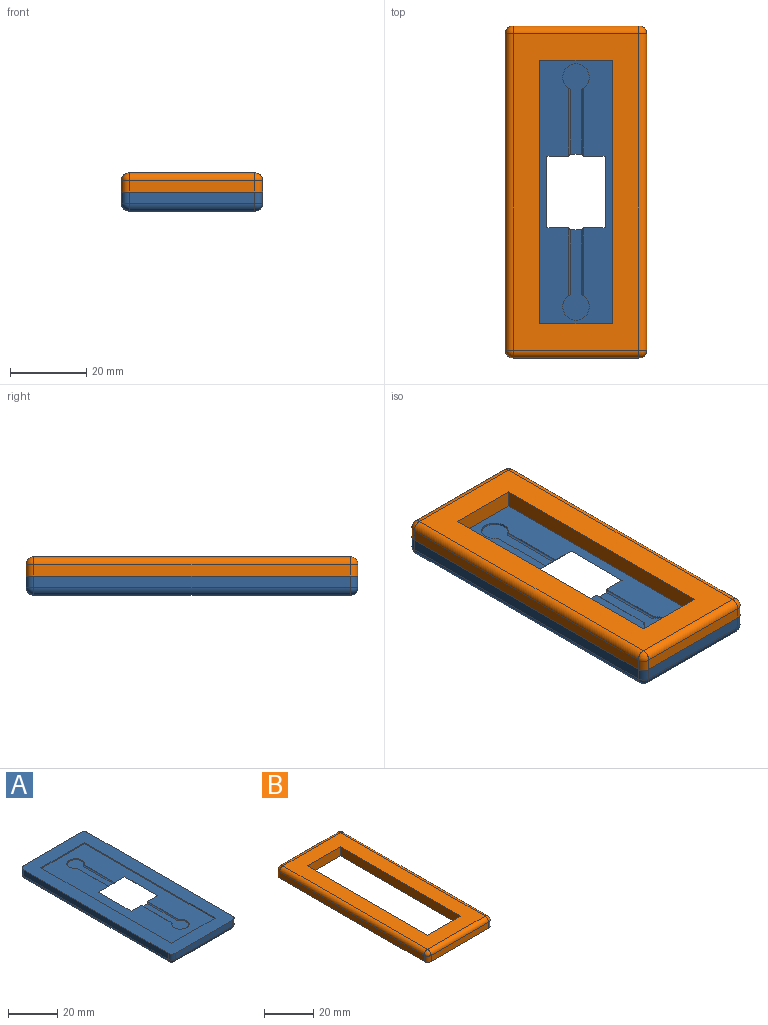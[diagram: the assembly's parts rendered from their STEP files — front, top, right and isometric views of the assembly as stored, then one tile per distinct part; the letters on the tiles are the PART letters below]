
ASSEMBLY  parts=2 mates=1
PART A: 35 faces, bbox 37x87x5 mm
  f0: plane 75x25mm, normal (0,0,1), area 1381.6mm2, adj f1,f2,f9,f10,f11,f12,f25,f26
  f1: plane 24.23x4.5mm, normal (0,0.71,-0.71), area 123.1mm2, adj f0,f3,f25,f26,f29,f31,f32
  f2: plane 24.23x4.5mm, normal (0,-0.71,-0.71), area 123.1mm2, adj f0,f3,f25,f26,f27,f33,f34
  f3: plane 83x33mm, normal (0,0,-1), area 2064.7mm2, adj f1,f2,f16,f17,f21,f22,f25,f26
  f4: plane 87x37mm, normal (0,0,1), area 1340.6mm2, adj f5,f6,f7,f8,f9,f10,f11,f12
  f5: plane 83x3mm, normal (1,0,0), area 249mm2, adj f4,f15,f21,f24
  f6: plane 33x3mm, normal (0,-1,0), area 99mm2, adj f4,f18,f22,f24
  f7: plane 83x3mm, normal (-1,0,0), area 249mm2, adj f4,f13,f17,f18
  f8: plane 33x3mm, normal (0,1,0), area 99mm2, adj f4,f13,f15,f16
  f9: plane 75x0.5mm, normal (-1,0,0), area 37.5mm2, adj f0,f4,f10,f12
  f10: plane 25x0.5mm, normal (0,-1,0), area 12.5mm2, adj f0,f4,f9,f11
  f11: plane 75x0.5mm, normal (1,0,0), area 37.5mm2, adj f0,f4,f10,f12
  f12: plane 25x0.5mm, normal (0,1,0), area 12.5mm2, adj f0,f4,f9,f11
  f13: cylinder r=2mm len=3mm, axis (0,0,-1), area 9.4mm2, adj f4,f7,f8,f14
  f14: sphere r=2mm, area 6.3mm2, adj f13,f16,f17
  f15: cylinder r=2mm len=3mm, axis (0,0,1), area 9.4mm2, adj f4,f5,f8,f19
  f16: cylinder r=2mm len=33mm, axis (-1,0,0), area 103.7mm2, adj f3,f8,f14,f19
  f17: cylinder r=2mm len=83mm, axis (0,-1,0), area 260.8mm2, adj f3,f7,f14,f20
  f18: cylinder r=2mm len=3mm, axis (0,0,1), area 9.4mm2, adj f4,f6,f7,f20
  f19: sphere r=2mm, area 6.3mm2, adj f15,f16,f21
  f20: sphere r=2mm, area 6.3mm2, adj f17,f18,f22
  f21: cylinder r=2mm len=83mm, axis (0,1,0), area 260.8mm2, adj f3,f5,f19,f23
  f22: cylinder r=2mm len=33mm, axis (1,0,0), area 103.7mm2, adj f3,f6,f20,f23
  f23: sphere r=2mm, area 6.3mm2, adj f21,f22,f24
  f24: cylinder r=2mm len=3mm, axis (0,0,-1), area 9.4mm2, adj f4,f5,f6,f23
  f25: plane 27.82x4.5mm, normal (-0.71,0,-0.71), area 148.4mm2, adj f0,f1,f2,f3
  f26: plane 27.82x4.5mm, normal (0.71,0,-0.71), area 148.4mm2, adj f0,f1,f2,f3
  f27: plane 23.67x6.97mm, normal (0,0,1), area 84.4mm2, adj f2,f28,f33,f34
  f28: cylinder r=3.48mm len=6.97mm, axis (0,0,1), area 9.1mm2, adj f0,f27,f33,f34
  f29: plane 23.67x6.97mm, normal (0,0,1), area 84.4mm2, adj f1,f30,f31,f32
  f30: cylinder r=3.48mm len=6.97mm, axis (0,0,1), area 9.1mm2, adj f0,f29,f31,f32
  f31: cylinder r=0.5mm len=17.75mm, axis (0,-1,0), area 13.6mm2, adj f0,f1,f29,f30
  f32: cylinder r=0.5mm len=17.75mm, axis (0,1,0), area 13.6mm2, adj f0,f1,f29,f30
  f33: cylinder r=0.5mm len=17.75mm, axis (0,-1,0), area 13.6mm2, adj f0,f2,f27,f28
  f34: cylinder r=0.5mm len=17.75mm, axis (0,1,0), area 13.6mm2, adj f0,f2,f27,f28
PART B: 37 faces, bbox 37x87x5 mm
  f0: plane 87x37mm, normal (0,0,-1), area 1212.6mm2, adj f1,f2,f3,f8,f10,f12,f15,f21
  f1: plane 33x3mm, normal (0,1,0), area 99mm2, adj f0,f12,f18,f21
  f2: plane 83x3mm, normal (-1,0,0), area 249mm2, adj f0,f15,f19,f21
  f3: plane 33x3mm, normal (0,-1,0), area 99mm2, adj f0,f10,f14,f15
  f4: plane 69x4.5mm, normal (1,0,0), area 310.5mm2, adj f5,f7,f9,f26
  f5: plane 19x4.5mm, normal (0,-1,0), area 85.5mm2, adj f4,f6,f9,f26
  f6: plane 69x4.5mm, normal (-1,0,0), area 310.5mm2, adj f5,f7,f9,f26
  f7: plane 19x4.5mm, normal (0,1,0), area 85.5mm2, adj f4,f6,f9,f26
  f8: plane 83x3mm, normal (1,0,0), area 249mm2, adj f0,f10,f12,f13
  f9: plane 83x33mm, normal (0,0,1), area 1428mm2, adj f4,f5,f6,f7,f13,f14,f18,f19
  f10: cylinder r=2mm len=3mm, axis (0,0,-1), area 9.4mm2, adj f0,f3,f8,f11
  f11: sphere r=2mm, area 6.3mm2, adj f10,f13,f14
  f12: cylinder r=2mm len=3mm, axis (0,0,-1), area 9.4mm2, adj f0,f1,f8,f16
  f13: cylinder r=2mm len=83mm, axis (0,-1,0), area 260.8mm2, adj f8,f9,f11,f16
  f14: cylinder r=2mm len=33mm, axis (-1,0,0), area 103.7mm2, adj f3,f9,f11,f17
  f15: cylinder r=2mm len=3mm, axis (0,0,-1), area 9.4mm2, adj f0,f2,f3,f17
  f16: sphere r=2mm, area 6.3mm2, adj f12,f13,f18
  f17: sphere r=2mm, area 6.3mm2, adj f14,f15,f19
  f18: cylinder r=2mm len=33mm, axis (1,0,0), area 103.7mm2, adj f1,f9,f16,f20
  f19: cylinder r=2mm len=83mm, axis (0,1,0), area 260.8mm2, adj f2,f9,f17,f20
  f20: sphere r=2mm, area 6.3mm2, adj f18,f19,f21
  f21: cylinder r=2mm len=3mm, axis (0,0,-1), area 9.4mm2, adj f0,f1,f2,f20
  f22: plane 25x0.5mm, normal (0,-1,0), area 12.5mm2, adj f0,f23,f25,f26
  f23: plane 75x0.5mm, normal (1,0,0), area 37.5mm2, adj f0,f22,f24,f26
  f24: plane 25x0.5mm, normal (0,1,0), area 12.5mm2, adj f0,f23,f25,f26
  f25: plane 75x0.5mm, normal (-1,0,0), area 37.5mm2, adj f0,f22,f24,f26
  f26: plane 75x25mm, normal (0,0,-1), area 564mm2, adj f4,f5,f6,f7,f22,f23,f24,f25
  f27: plane 3.35x3.35mm, normal (1,0,0), area 11.2mm2, adj f0,f28,f30,f31
  f28: plane 19.1x3.35mm, normal (0,-1,0), area 64mm2, adj f0,f27,f29,f31
  f29: plane 3.35x3.35mm, normal (-1,0,0), area 11.2mm2, adj f0,f28,f30,f31
  f30: plane 19.1x3.35mm, normal (0,1,0), area 64mm2, adj f0,f27,f29,f31
  f31: plane 19.1x3.35mm, normal (0,0,-1), area 64mm2, adj f27,f28,f29,f30
  f32: plane 3.35x3.35mm, normal (1,0,0), area 11.2mm2, adj f0,f33,f35,f36
  f33: plane 19.1x3.35mm, normal (0,-1,0), area 64mm2, adj f0,f32,f34,f36
  f34: plane 3.35x3.35mm, normal (-1,0,0), area 11.2mm2, adj f0,f33,f35,f36
  f35: plane 19.1x3.35mm, normal (0,1,0), area 64mm2, adj f0,f32,f34,f36
  f36: plane 19.1x3.35mm, normal (0,0,-1), area 64mm2, adj f32,f33,f34,f35
PLACE A t=(0,0,11)mm
PLACE B at identity
MATE fastened A.f4 <-> B.f0  axis (0,0,1) through (18.5,0,5.5)mm
